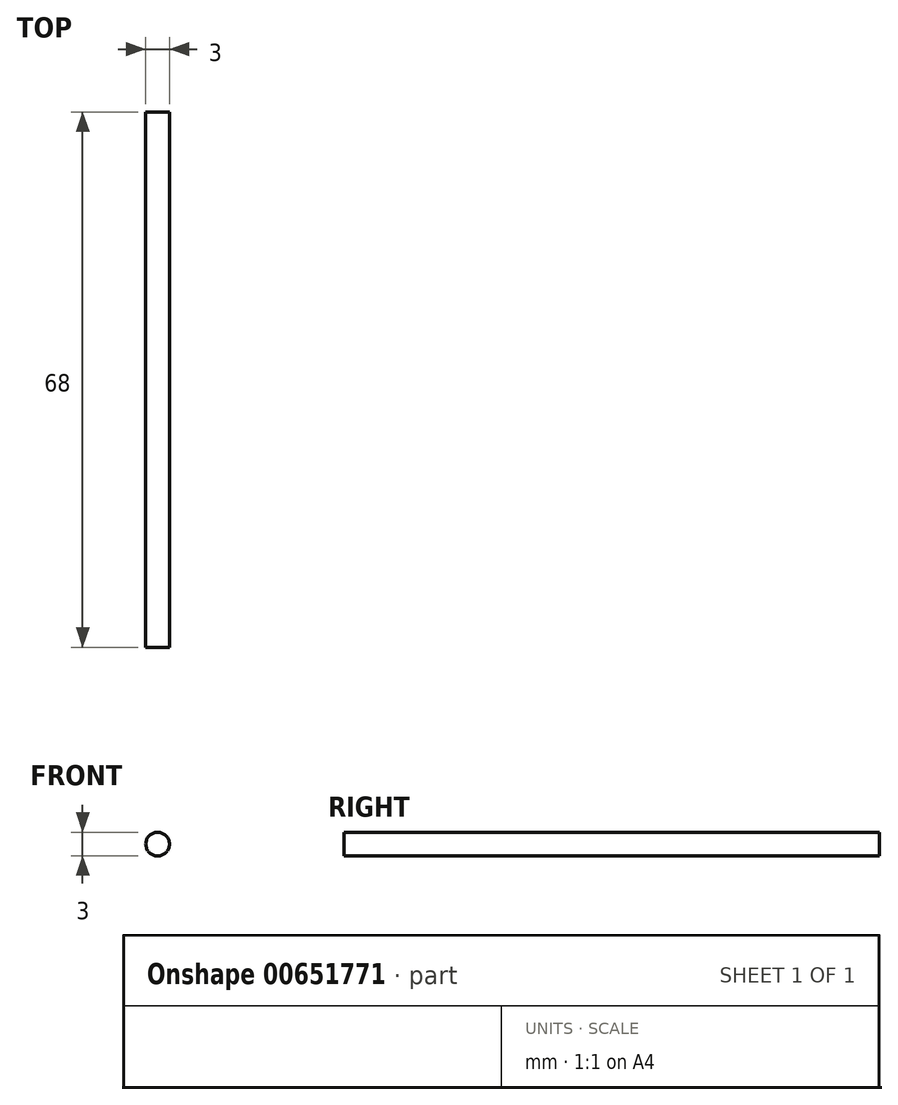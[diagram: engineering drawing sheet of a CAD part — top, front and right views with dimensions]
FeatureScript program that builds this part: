
annotation { "Feature Type Name" : "Feature", "Feature Type Description" : "" }
export const myFeature = defineFeature(function(context is Context, id is Id, definition is map)
    precondition{}
    {
        {
            var Q0;
            Q0=qCreatedBy(makeId("Front.planeOp"),FACE);
            var sketch = newSketch(context, id + "F0", { "sketchPlane" : qUnion([Q0])});
            skCircle(sketch, "E0", {"center": v(0, 0) * mm, "radius": 1.5 * mm});
            skSolve(sketch);
        }
        {
            var Q0;
            Q0 = qSketchRegion(id + "F0", true);
            extrude(context, id + "F1", {"entities" : qUnion([Q0]), "endBound" : BoundingType.SYMMETRIC, "depth" : 68 * mm, "offsetDistance" : 25 * mm});
        }
    });
